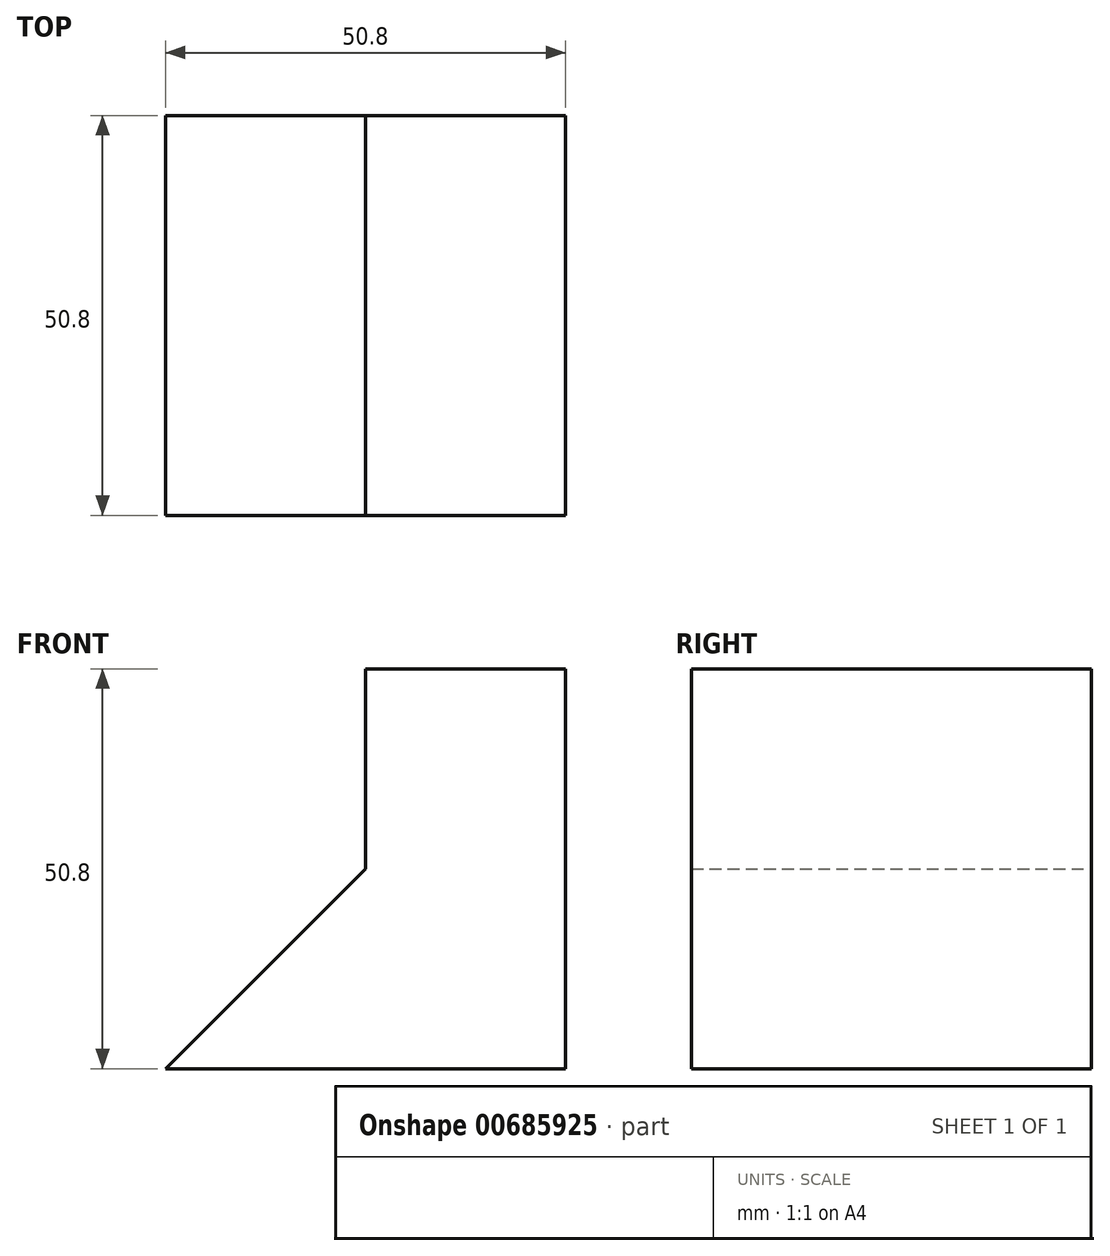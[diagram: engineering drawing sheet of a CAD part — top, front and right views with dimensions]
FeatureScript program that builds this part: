
annotation { "Feature Type Name" : "Feature", "Feature Type Description" : "" }
export const myFeature = defineFeature(function(context is Context, id is Id, definition is map)
    precondition{}
    {
        {
            var Q0;
            Q0=qCreatedBy(makeId("Front.planeOp"),FACE);
            var sketch = newSketch(context, id + "F0", { "sketchPlane" : qUnion([Q0])});
            skLineSegment(sketch, "E0", {"start": v(0, 0) * mm, "end": v(0, 25.4) * mm});
            skLineSegment(sketch, "E1", {"start": v(0, 25.4) * mm, "end": v(25.4, 25.4) * mm});
            skLineSegment(sketch, "E2", {"start": v(25.4, 25.4) * mm, "end": v(25.4, -25.4) * mm});
            skLineSegment(sketch, "E3", {"start": v(25.4, -25.4) * mm, "end": v(-25.4, -25.4) * mm});
            skLineSegment(sketch, "E4", {"start": v(0, 0) * mm, "end": v(-25.4, -25.4) * mm});
            skSolve(sketch);
        }
        {
            var Q0;
            Q0 = qSketchRegion(id + "F0", true);
            extrude(context, id + "F1", {"entities" : qUnion([Q0]), "depth" : 50.8 * mm, "offsetDistance" : 25.4 * mm});
        }
    });
